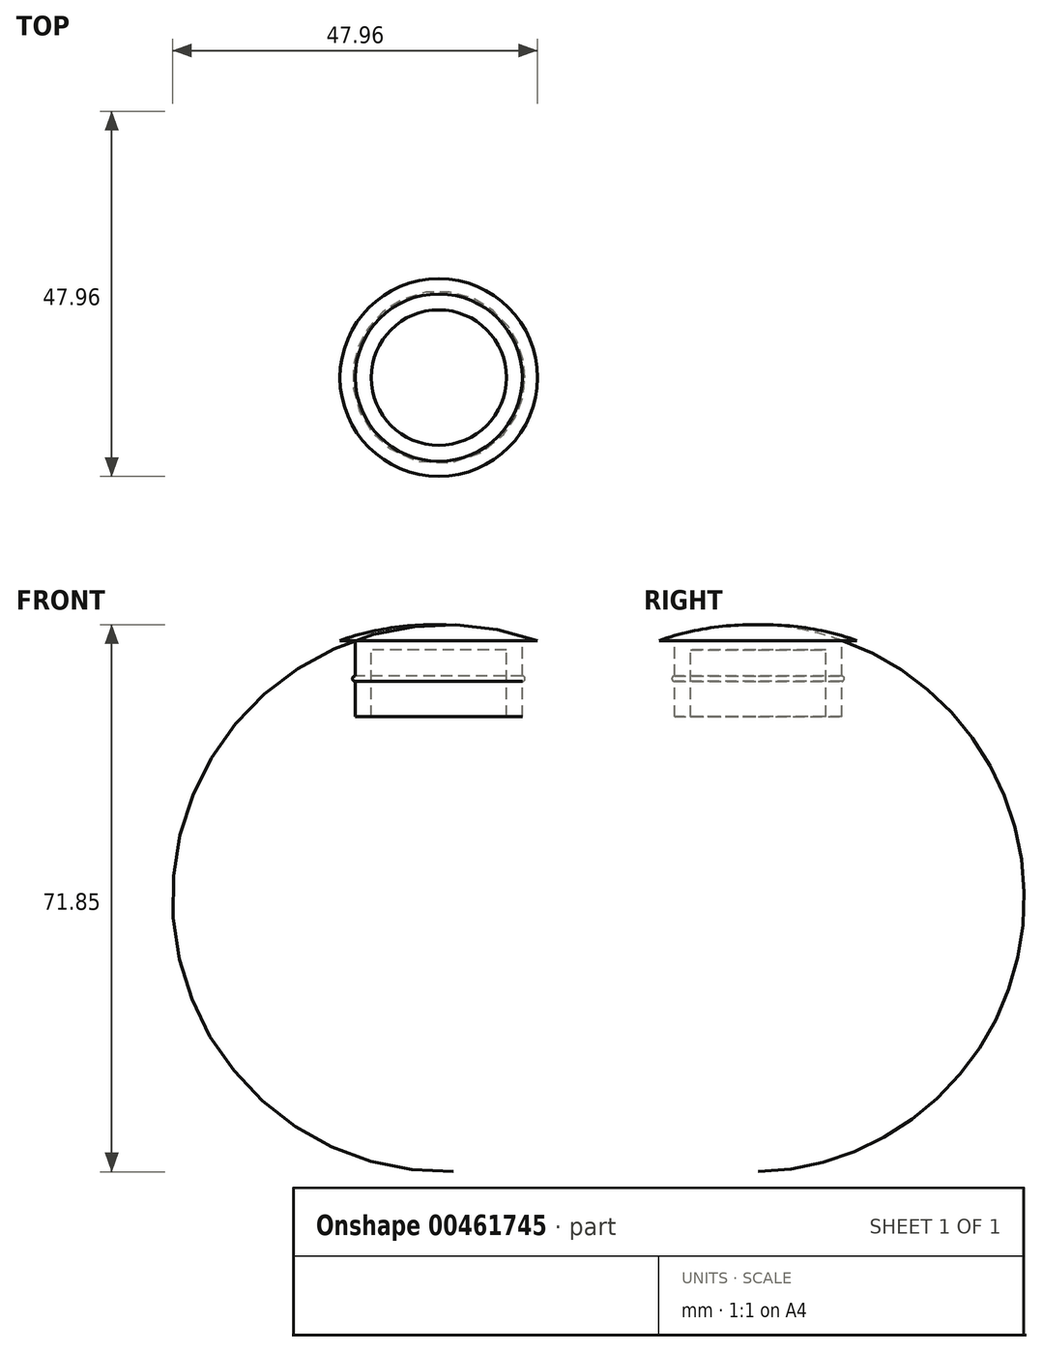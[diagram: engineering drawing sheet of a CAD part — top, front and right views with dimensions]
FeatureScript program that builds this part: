
annotation { "Feature Type Name" : "Feature", "Feature Type Description" : "" }
export const myFeature = defineFeature(function(context is Context, id is Id, definition is map)
    precondition{}
    {
        {
            var Q0;
            Q0=qCreatedBy(makeId("Right.planeOp"),FACE);
            var sketch = newSketch(context, id + "F0", { "sketchPlane" : qUnion([Q0])});
            skLineSegment(sketch, "E0.left", {"start": v(0, 0) * mm, "end": v(0, -10) * mm, "construction": true});
            skLineSegment(sketch, "E0.right", {"start": v(10.98, 0) * mm, "end": v(10.98, -10) * mm});
            skPoint(sketch, "E1.startSnap0", {"position": v(5.5, 0) * mm});
            skLineSegment(sketch, "E2", {"start": v(10.98, 0) * mm, "end": v(12.98, 0) * mm});
            skLineSegment(sketch, "E3", {"start": v(0, 0) * mm, "end": v(0, 2.06) * mm, "construction": true});
            skArc(sketch, "E4", {"start": v(12.98, 0) * mm, "mid": v(6.58, 1.63) * mm, "end": v(0, 2.06) * mm});
            skArc(sketch, "E5", {"start": v(10.98, -5.35) * mm, "mid": v(11.33, -5) * mm, "end": v(10.98, -4.65) * mm});
            skLineSegment(sketch, "E6", {"start": v(10.98, -10) * mm, "end": v(8.9, -10) * mm});
            skLineSegment(sketch, "E7", {"start": v(8.9, -10) * mm, "end": v(8.9, -1.25) * mm});
            skLineSegment(sketch, "E8", {"start": v(8.9, -1.25) * mm, "end": v(0, -1.25) * mm});
            skLineSegment(sketch, "E9", {"start": v(0, 2.06) * mm, "end": v(0, -1.25) * mm});
            skSolve(sketch);
        }
        {
            var Q0;
            {var subQ0=sQuery(id+"F0.wireOp",EDGE,"E2");Q0=makeQuery(id+"F0.imprint","IMPRINT",FACE,{"disambiguationData":[TD([[makeQuery(id+"F0.imprint","IMPRINT",EDGE,{"derivedFrom":subQ0}),1.0]])]});}
            var Q1;
            {var subQ0=sQuery(id+"F0.wireOp",EDGE,"E5");Q1=makeQuery(id+"F0.imprint","IMPRINT",FACE,{"disambiguationData":[TD([[makeQuery(id+"F0.imprint","IMPRINT",EDGE,{"derivedFrom":subQ0}),1.0]])]});}
            var Q2;
            Q2=sQuery(id+"F0.wireOp",EDGE,"E9");
            revolve(context, id + "F1", {"entities" : qUnion([Q0, Q1]), "axis" : qUnion([Q2]), "revolveType" : RevolveType.FULL});
        }
    });
